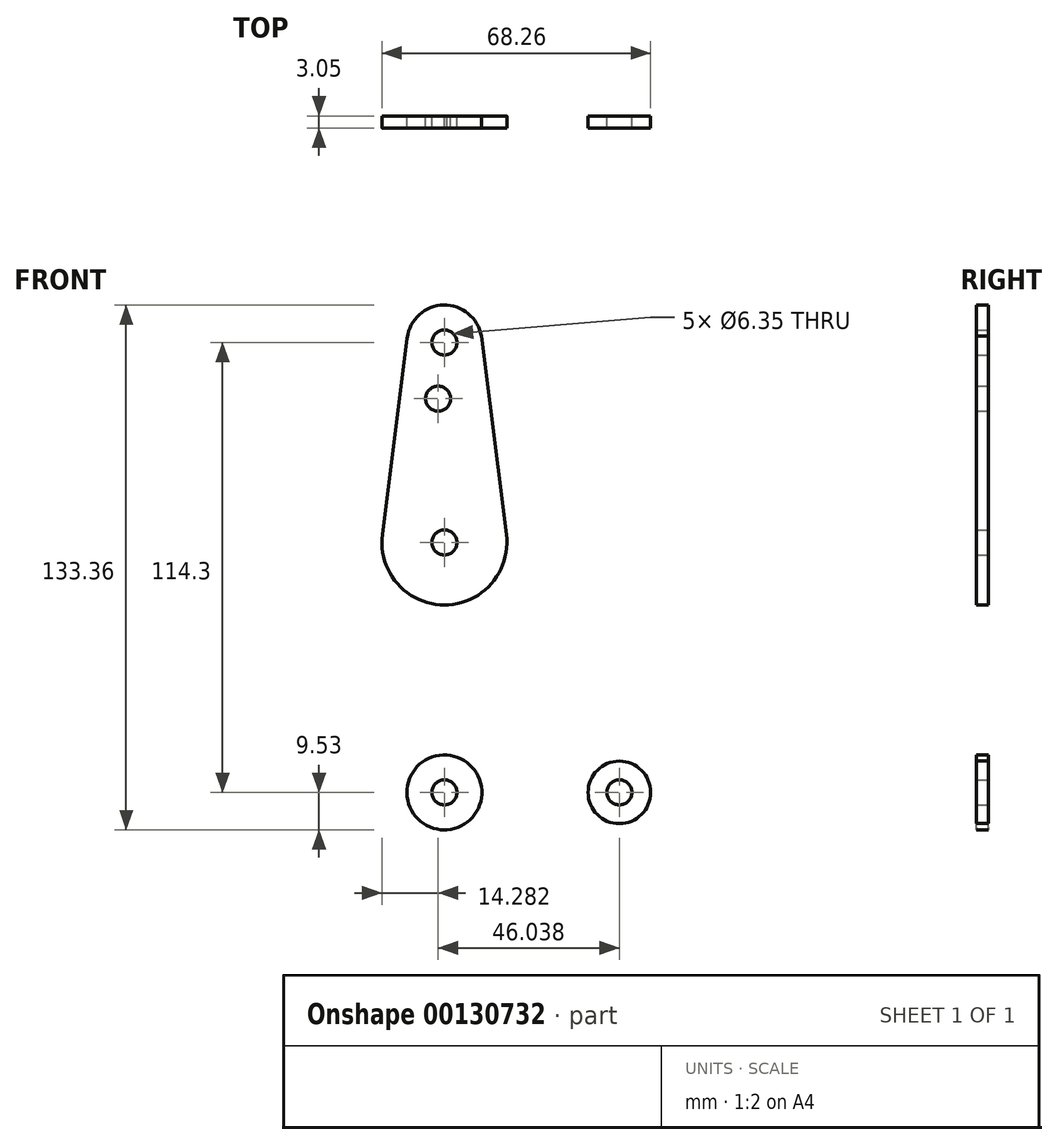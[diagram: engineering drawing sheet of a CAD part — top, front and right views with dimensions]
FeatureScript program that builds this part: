
annotation { "Feature Type Name" : "Feature", "Feature Type Description" : "" }
export const myFeature = defineFeature(function(context is Context, id is Id, definition is map)
    precondition{}
    {
        {
            var Q0;
            Q0=qCreatedBy(makeId("Front.planeOp"),FACE);
            var sketch = newSketch(context, id + "F0", { "sketchPlane" : qUnion([Q0])});
            skCircle(sketch, "E0", {"center": v(0, 114.3) * mm, "radius": 9.53 * mm});
            skCircle(sketch, "E1", {"center": v(0, 63.5) * mm, "radius": 15.88 * mm});
            skCircle(sketch, "E2", {"center": v(0, 0) * mm, "radius": 9.53 * mm});
            skLineSegment(sketch, "E3", {"start": v(0, 114.3) * mm, "end": v(0, 0) * mm, "construction": true});
            skLineSegment(sketch, "E4", {"start": v(0, 0) * mm, "end": v(44.45, 0) * mm, "construction": true});
            skCircle(sketch, "E5", {"center": v(44.45, 0) * mm, "radius": 7.94 * mm});
            skLineSegment(sketch, "E6", {"start": v(-9.45, 115.5) * mm, "end": v(-15.75, 65.48) * mm});
            skLineSegment(sketch, "E7", {"start": v(-15.8, 61.91) * mm, "end": v(-9.57, 0) * mm});
            skLineSegment(sketch, "E8", {"start": v(18.94, 8.85) * mm, "end": v(44.73, 7.93) * mm});
            skLineSegment(sketch, "E9", {"start": v(0, -9.53) * mm, "end": v(44.73, -7.93) * mm});
            skCircle(sketch, "E10", {"center": v(0, 114.3) * mm, "radius": 3.18 * mm});
            skCircle(sketch, "E11", {"center": v(0, 63.5) * mm, "radius": 3.18 * mm});
            skCircle(sketch, "E12", {"center": v(0, 0) * mm, "radius": 3.18 * mm});
            skCircle(sketch, "E13", {"center": v(44.45, 0) * mm, "radius": 3.18 * mm});
            skCircle(sketch, "E14", {"center": v(-1.59, 100.03) * mm, "radius": 3.18 * mm});
            skLineSegment(sketch, "E15", {"start": v(9.4, 115.9) * mm, "end": v(15.75, 65.49) * mm});
            skLineSegment(sketch, "E16", {"start": v(11.31, 17.6) * mm, "end": v(15.8, 61.9) * mm});
            skPoint(sketch, "E17.newPointA", {"position": v(9.53, 0) * mm});
            skArc(sketch, "E17.filletArc", {"start": v(11.31, 17.6) * mm, "mid": v(13.23, 11.57) * mm, "end": v(18.94, 8.85) * mm});
            skSolve(sketch);
        }
        {
            var Q0;
            {var subQ0=sQuery(id+"F0.wireOp",EDGE,"E15");var subQ1=sQuery(id+"F0.wireOp",EDGE,"E0");var subQ2=makeQuery(id+"F0.imprint","INTERSECT",VERTEX,{"disambiguationData":[OD(0.0)],"derivedFrom":[subQ1,subQ0]});Q0=makeQuery(id+"F0.imprint","IMPRINT",FACE,{"disambiguationData":[TD([[makeQuery(id+"F0.imprint","IMPRINT",EDGE,{"disambiguationData":[TD([[subQ2,1.0]])],"derivedFrom":subQ1}),1.0]])]});}
            var Q1;
            {var subQ0=sQuery(id+"F0.wireOp",EDGE,"E9");var subQ1=sQuery(id+"F0.wireOp",EDGE,"E2");var subQ2=makeQuery(id+"F0.imprint","INTERSECT",VERTEX,{"disambiguationData":[OD(0.0)],"derivedFrom":[subQ1,subQ0]});Q1=makeQuery(id+"F0.imprint","IMPRINT",FACE,{"disambiguationData":[TD([[makeQuery(id+"F0.imprint","IMPRINT",EDGE,{"disambiguationData":[TD([[subQ2,-1.0]])],"derivedFrom":subQ1}),1.0]])]});}
            var Q2;
            Q2=makeQuery(id+"F0.imprint","IMPRINT",FACE,{"disambiguationData":[TD([[makeQuery(id+"F0.imprint","IMPRINT",EDGE,{"derivedFrom":sQuery(id+"F0.wireOp",EDGE,"E13")}),-1.0]])]});
            var Q3;
            Q3=makeQuery(id+"F0.imprint","IMPRINT",FACE,{"disambiguationData":[TD([[makeQuery(id+"F0.imprint","IMPRINT",EDGE,{"derivedFrom":sQuery(id+"F0.wireOp",EDGE,"E11")}),-1.0]])]});
            var Q4;
            Q4=makeQuery(id+"F0.imprint","IMPRINT",FACE,{"disambiguationData":[TD([[makeQuery(id+"F0.imprint","IMPRINT",EDGE,{"derivedFrom":sQuery(id+"F0.wireOp",EDGE,"E12")}),-1.0]])]});
            var Q5;
            Q5=makeQuery(id+"F0.imprint","IMPRINT",FACE,{"disambiguationData":[TD([[makeQuery(id+"F0.imprint","IMPRINT",EDGE,{"derivedFrom":sQuery(id+"F0.wireOp",EDGE,"E10")}),-1.0]])]});
            var Q6;
            {var subQ0=sQuery(id+"F0.wireOp",EDGE,"E6");Q6=makeQuery(id+"F0.imprint","IMPRINT",FACE,{"disambiguationData":[TD([[makeQuery(id+"F0.imprint","IMPRINT",EDGE,{"derivedFrom":subQ0}),1.0]])]});}
            extrude(context, id + "F1", {"entities" : qUnion([Q0, Q1, Q2, Q3, Q4, Q5, Q6]), "depth" : 3.05 * mm});
        }
    });
